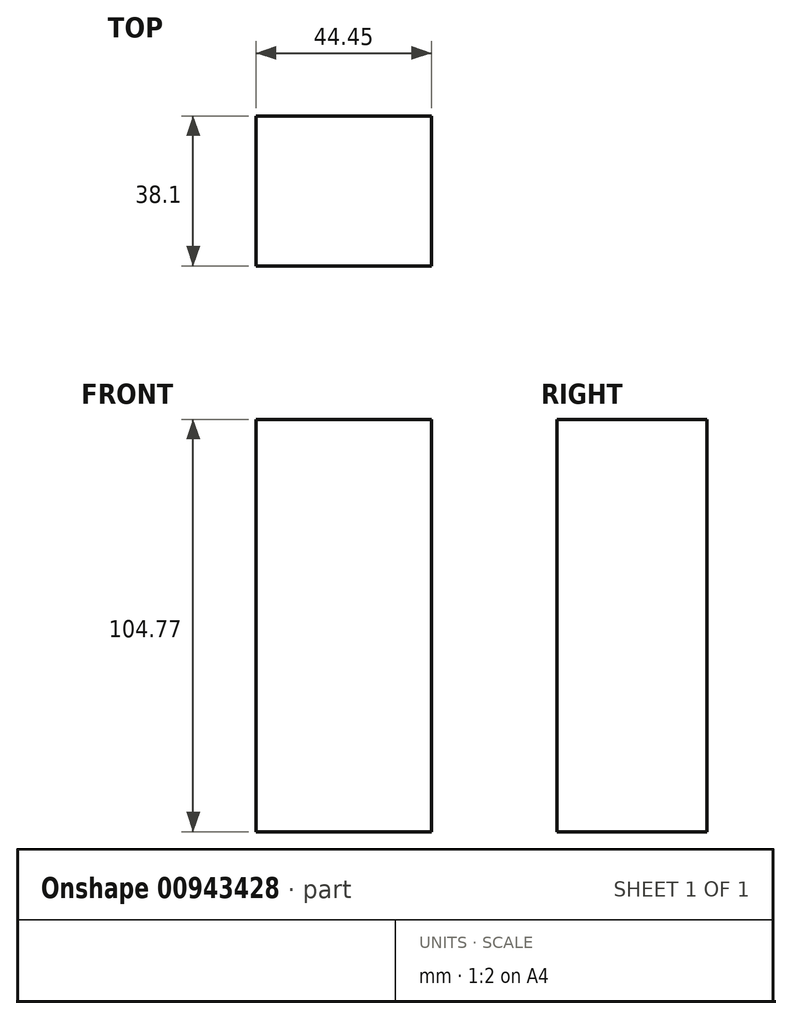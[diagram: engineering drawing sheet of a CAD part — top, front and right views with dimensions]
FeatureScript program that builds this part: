
annotation { "Feature Type Name" : "Feature", "Feature Type Description" : "" }
export const myFeature = defineFeature(function(context is Context, id is Id, definition is map)
    precondition{}
    {
        {
            var Q0;
            Q0=qCreatedBy(makeId("Top.planeOp"),FACE);
            var sketch = newSketch(context, id + "F0", { "sketchPlane" : qUnion([Q0])});
            skLineSegment(sketch, "E0.bottom", {"start": v(0, 0) * mm, "end": v(-44.45, 0) * mm});
            skLineSegment(sketch, "E0.top", {"start": v(0, 38.1) * mm, "end": v(-44.45, 38.1) * mm});
            skLineSegment(sketch, "E0.left", {"start": v(0, 0) * mm, "end": v(0, 38.1) * mm});
            skLineSegment(sketch, "E0.right", {"start": v(-44.45, 0) * mm, "end": v(-44.45, 38.1) * mm});
            skSolve(sketch);
        }
        {
            var Q0;
            Q0=makeQuery(id+"F0.imprint","IMPRINT",FACE,{"disambiguationData":[TD([[makeQuery(id+"F0.imprint","IMPRINT",EDGE,{"derivedFrom":sQuery(id+"F0.wireOp",EDGE,"E0.bottom")}),-1.0]])]});
            extrude(context, id + "F1", {"entities" : qUnion([Q0]), "depth" : 104.77 * mm, "offsetDistance" : 25.4 * mm});
        }
    });
